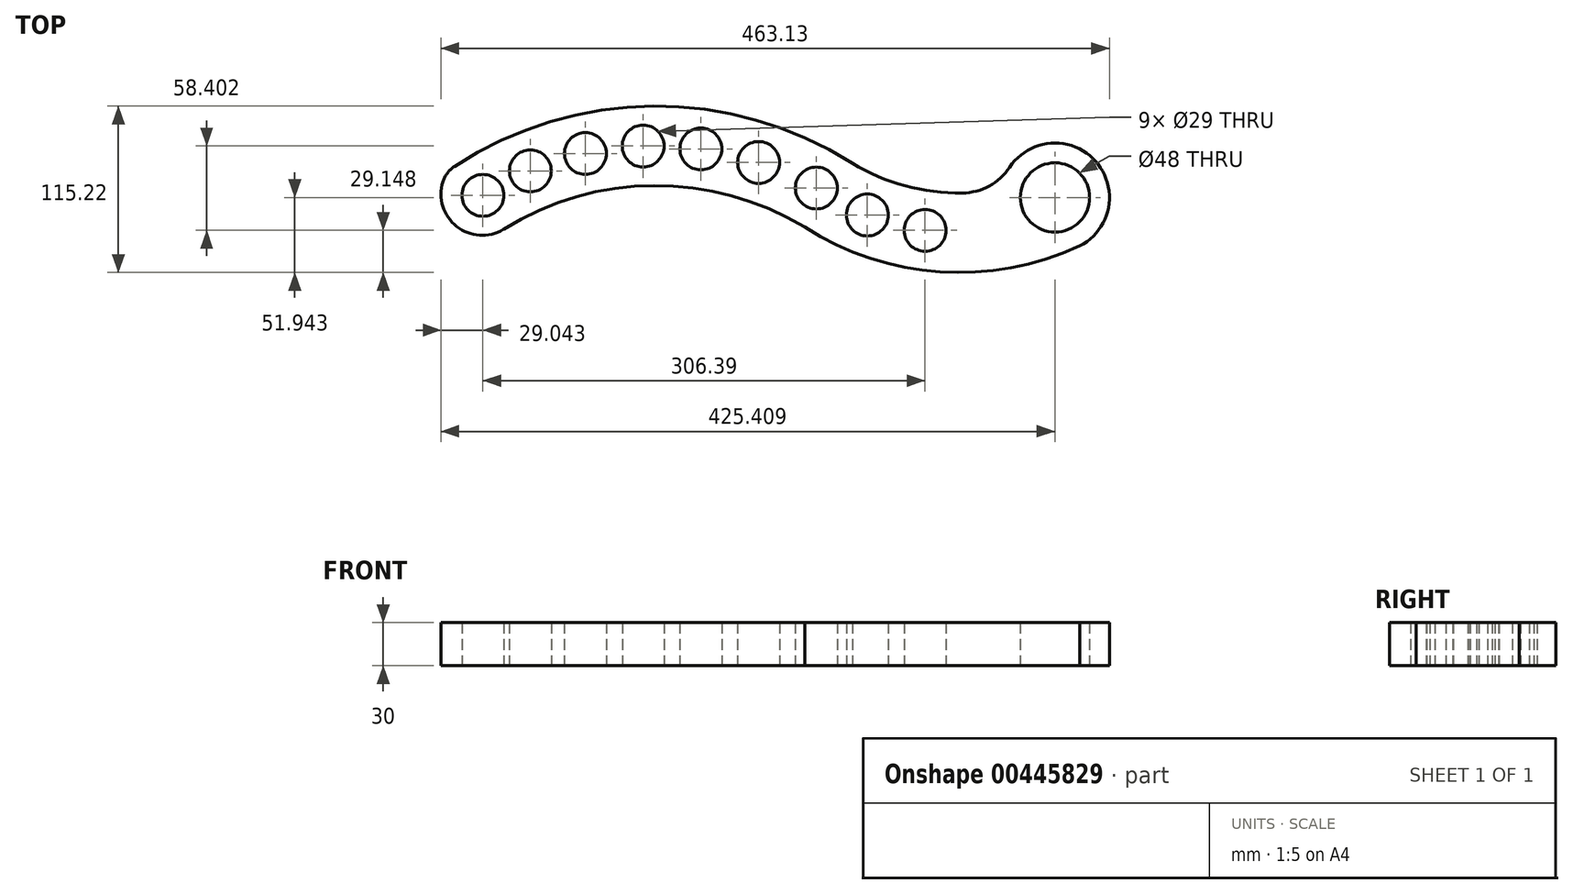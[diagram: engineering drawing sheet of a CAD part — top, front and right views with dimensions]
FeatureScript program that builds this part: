
annotation { "Feature Type Name" : "Feature", "Feature Type Description" : "" }
export const myFeature = defineFeature(function(context is Context, id is Id, definition is map)
    precondition{}
    {
        {
            var Q0;
            Q0=qCreatedBy(makeId("Top.planeOp"),FACE);
            var sketch = newSketch(context, id + "F0", { "sketchPlane" : qUnion([Q0])});
            skArc(sketch, "E0", {"start": v(208.17, 1.13) * mm, "mid": v(103.7, 30) * mm, "end": v(-0.37, -0.23) * mm});
            skArc(sketch, "E1", {"start": v(208.17, 1.13) * mm, "mid": v(301.84, -29.77) * mm, "end": v(398.82, -11.82) * mm});
            skLineSegment(sketch, "E2", {"start": v(106.57, 30) * mm, "end": v(434.27, 24.83) * mm, "construction": true});
            skPoint(sketch, "E2.startSnap0", {"position": v(105, 30) * mm});
            skLineSegment(sketch, "E3", {"start": v(431.17, -30) * mm, "end": v(-36.86, -30) * mm, "construction": true});
            skPoint(sketch, "E3.startSnap0", {"position": v(305.92, -30) * mm});
            skPoint(sketch, "E3.endSnap0", {"position": v(305.92, -30) * mm});
            skArc(sketch, "E4.0", {"start": v(241.16, 45.37) * mm, "mid": v(103.05, 85) * mm, "end": v(-34.45, 43.25) * mm});
            skArc(sketch, "E4.1", {"start": v(241.16, 45.37) * mm, "mid": v(277.88, 29.74) * mm, "end": v(317.47, 24.8) * mm});
            skArc(sketch, "E5", {"start": v(-42.56, 32.46) * mm, "mid": v(-32.95, 1.62) * mm, "end": v(-0.71, -0.44) * mm});
            skArc(sketch, "E6.0", {"start": v(226.67, 22) * mm, "mid": v(106.27, 57.5) * mm, "end": v(-14.53, 23.35) * mm});
            skArc(sketch, "E6.1", {"start": v(226.67, 22) * mm, "mid": v(316.31, -2.72) * mm, "end": v(405.65, 23.05) * mm});
            skCircle(sketch, "E7", {"center": v(-14.8, 23.18) * mm, "radius": 14.5 * mm});
            skCircle(sketch, "E8", {"center": v(56.23, 52.18) * mm, "radius": 14.5 * mm});
            skCircle(sketch, "E9", {"center": v(18.09, 40.14) * mm, "radius": 14.5 * mm});
            skCircle(sketch, "E10", {"center": v(96.23, 57.33) * mm, "radius": 14.5 * mm});
            skCircle(sketch, "E11", {"center": v(136.23, 55.33) * mm, "radius": 14.5 * mm});
            skCircle(sketch, "E12", {"center": v(176.23, 46) * mm, "radius": 14.5 * mm});
            skCircle(sketch, "E13", {"center": v(216.23, 28.27) * mm, "radius": 14.5 * mm});
            skCircle(sketch, "E14", {"center": v(251.6, 9.57) * mm, "radius": 14.5 * mm});
            skCircle(sketch, "E15", {"center": v(291.6, -1.07) * mm, "radius": 14.5 * mm});
            skCircle(sketch, "E16", {"center": v(381.57, 21.72) * mm, "radius": 24 * mm});
            skPoint(sketch, "E17.visualSharp", {"position": v(-38.64, 40.43) * mm});
            skArc(sketch, "E17.filletArc", {"start": v(-34.45, 43.25) * mm, "mid": v(-39.44, 38.56) * mm, "end": v(-42.56, 32.46) * mm});
            skPoint(sketch, "E18.visualSharp", {"position": v(0, 0) * mm});
            skArc(sketch, "E18.filletArc", {"start": v(-0.71, -0.44) * mm, "mid": v(-0.54, -0.34) * mm, "end": v(-0.37, -0.23) * mm});
            skArc(sketch, "E19", {"start": v(398.82, -11.82) * mm, "mid": v(409.7, 46.86) * mm, "end": v(350.17, 42.63) * mm});
            skPoint(sketch, "E20.visualSharp", {"position": v(344.33, 27.74) * mm});
            skArc(sketch, "E20.filletArc", {"start": v(317.47, 24.8) * mm, "mid": v(336.02, 29.67) * mm, "end": v(350.17, 42.63) * mm});
            skSolve(sketch);
        }
        {
            var Q0;
            Q0=makeQuery(id+"F0.imprint","IMPRINT",FACE,{"disambiguationData":[TD([[makeQuery(id+"F0.imprint","IMPRINT",EDGE,{"derivedFrom":sQuery(id+"F0.wireOp",EDGE,"E0")}),-1.0]])]});
            extrude(context, id + "F1", {"entities" : qUnion([Q0]), "depth" : 30 * mm});
        }
    });
